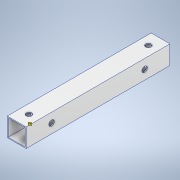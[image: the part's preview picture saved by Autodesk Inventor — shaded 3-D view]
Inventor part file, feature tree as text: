
AUTODESK INVENTOR PART (.ipt)
format: ipt  version: 2020.2 (Build 242310000, 310)  size: 149,504 bytes
history: native  units: mm
features: sketch x3, hole x2, extrude x1
ambient origin geometry x8: Origin, YZ Plane, XZ Plane, XY Plane, X Axis, Y Axis, Z Axis, Center Point
bodies: Solido1 (feature_tree)
feature tree (6):
  extrude  "Estrusione1"  Depth=20.0mm
  hole  "Foro7"  [1 undecoded]
  hole  "Foro8"  [1 undecoded]
  sketch  "Schizzo1"
  sketch  "Schizzo8"
  sketch  "Schizzo9"
note: 2 required parameter values undecoded (feature->parameter linkage not recoverable at this tier; creation-order binding heuristic only, values carry confidence <= 0.55)
